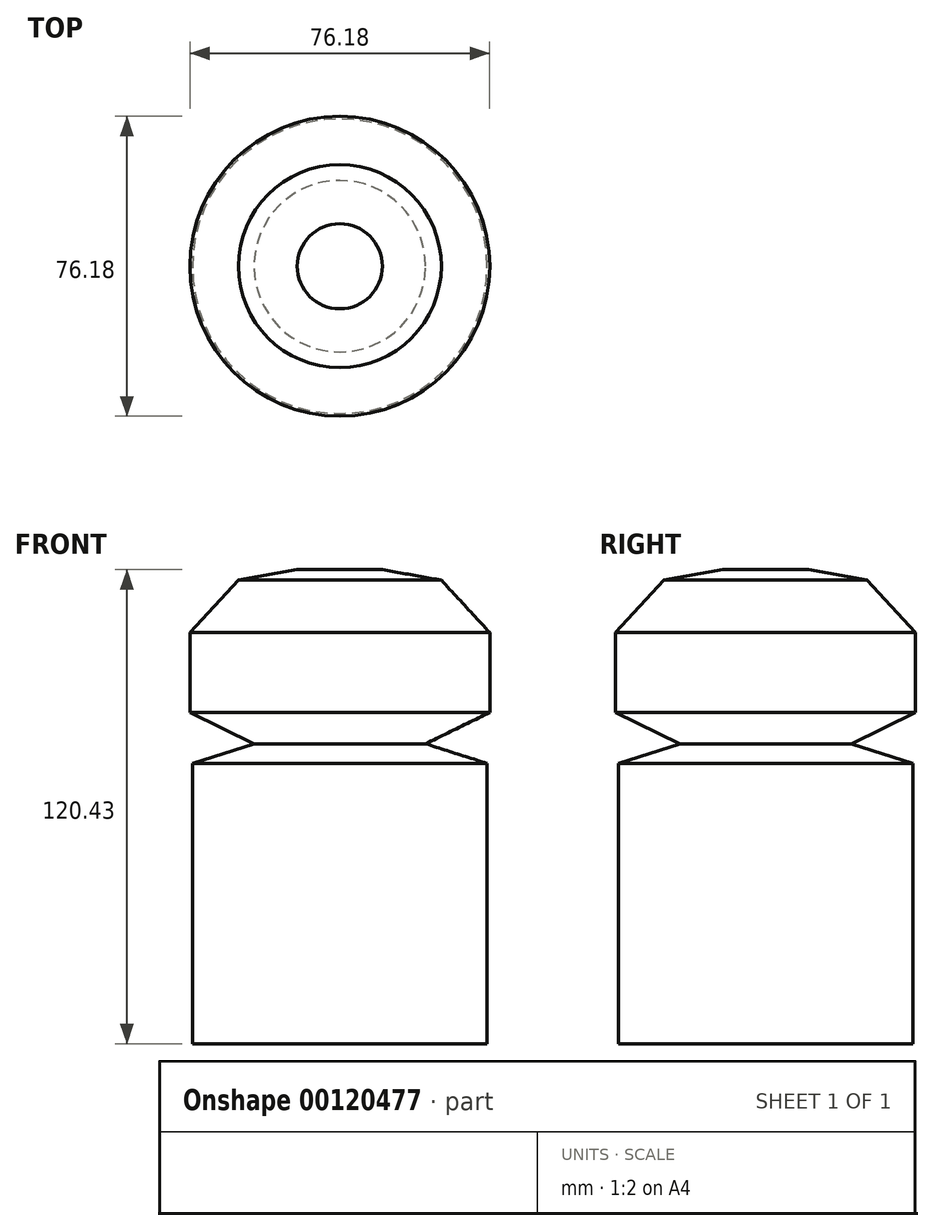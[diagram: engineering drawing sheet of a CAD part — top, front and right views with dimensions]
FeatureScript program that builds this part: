
annotation { "Feature Type Name" : "Feature", "Feature Type Description" : "" }
export const myFeature = defineFeature(function(context is Context, id is Id, definition is map)
    precondition{}
    {
        {
            var Q0;
            Q0=qCreatedBy(makeId("Front.planeOp"),FACE);
            var sketch = newSketch(context, id + "F0", { "sketchPlane" : qUnion([Q0])});
            skLineSegment(sketch, "E0", {"start": v(0, -51.07) * mm, "end": v(-37.43, -51.07) * mm});
            skLineSegment(sketch, "E1", {"start": v(-37.43, -51.07) * mm, "end": v(-37.43, 20.12) * mm});
            skLineSegment(sketch, "E2", {"start": v(-37.43, 20.12) * mm, "end": v(-21.8, 25.11) * mm});
            skLineSegment(sketch, "E3", {"start": v(-21.8, 25.11) * mm, "end": v(-38.1, 33.1) * mm});
            skLineSegment(sketch, "E4", {"start": v(-38.1, 33.1) * mm, "end": v(-38.1, 53.4) * mm});
            skLineSegment(sketch, "E5", {"start": v(-38.1, 53.4) * mm, "end": v(-25.78, 66.7) * mm});
            skLineSegment(sketch, "E6", {"start": v(-25.78, 66.7) * mm, "end": v(-10.81, 69.36) * mm});
            skLineSegment(sketch, "E7", {"start": v(-10.81, 69.36) * mm, "end": v(0, 69.36) * mm});
            skLineSegment(sketch, "E8", {"start": v(0, 69.36) * mm, "end": v(0, -51.07) * mm});
            skSolve(sketch);
        }
        {
            var Q0;
            Q0=makeQuery(id+"F0.imprint","IMPRINT",FACE,{"disambiguationData":[TD([[makeQuery(id+"F0.imprint","IMPRINT",EDGE,{"derivedFrom":sQuery(id+"F0.wireOp",EDGE,"E0")}),-1.0]])]});
            var Q1;
            Q1=sQuery(id+"F0.wireOp",EDGE,"E5");
            var Q2;
            Q2=sQuery(id+"F0.wireOp",EDGE,"E3");
            var Q3;
            Q3=sQuery(id+"F0.wireOp",EDGE,"E1");
            var Q4;
            Q4=sQuery(id+"F0.wireOp",EDGE,"E6");
            var Q5;
            Q5=sQuery(id+"F0.wireOp",EDGE,"E2");
            var Q6;
            Q6=sQuery(id+"F0.wireOp",EDGE,"E0");
            var Q7;
            Q7=sQuery(id+"F0.wireOp",EDGE,"Giu5DV5p-umtl-aB5Y-72Yc-DPGbrl5aIGpk");
            var Q8;
            Q8=sQuery(id+"F0.wireOp",EDGE,"E7");
            var Q9;
            Q9=sQuery(id+"F0.wireOp",EDGE,"E4");
            var Q10;
            Q10=sQuery(id+"F0.wireOp",EDGE,"FmvOLLeD-Wfjb-r1rO-V3XQ-fKaxgPzeuAWt");
            var Q11;
            Q11=sQuery(id+"F0.wireOp",EDGE,"E8");
            revolve(context, id + "F1", {"entities" : qUnion([Q0]), "surfaceEntities" : qUnion([Q1, Q2, Q3, Q4, Q5, Q6, Q7, Q8, Q9, Q10]), "axis" : qUnion([Q11]), "revolveType" : RevolveType.FULL});
        }
    });
